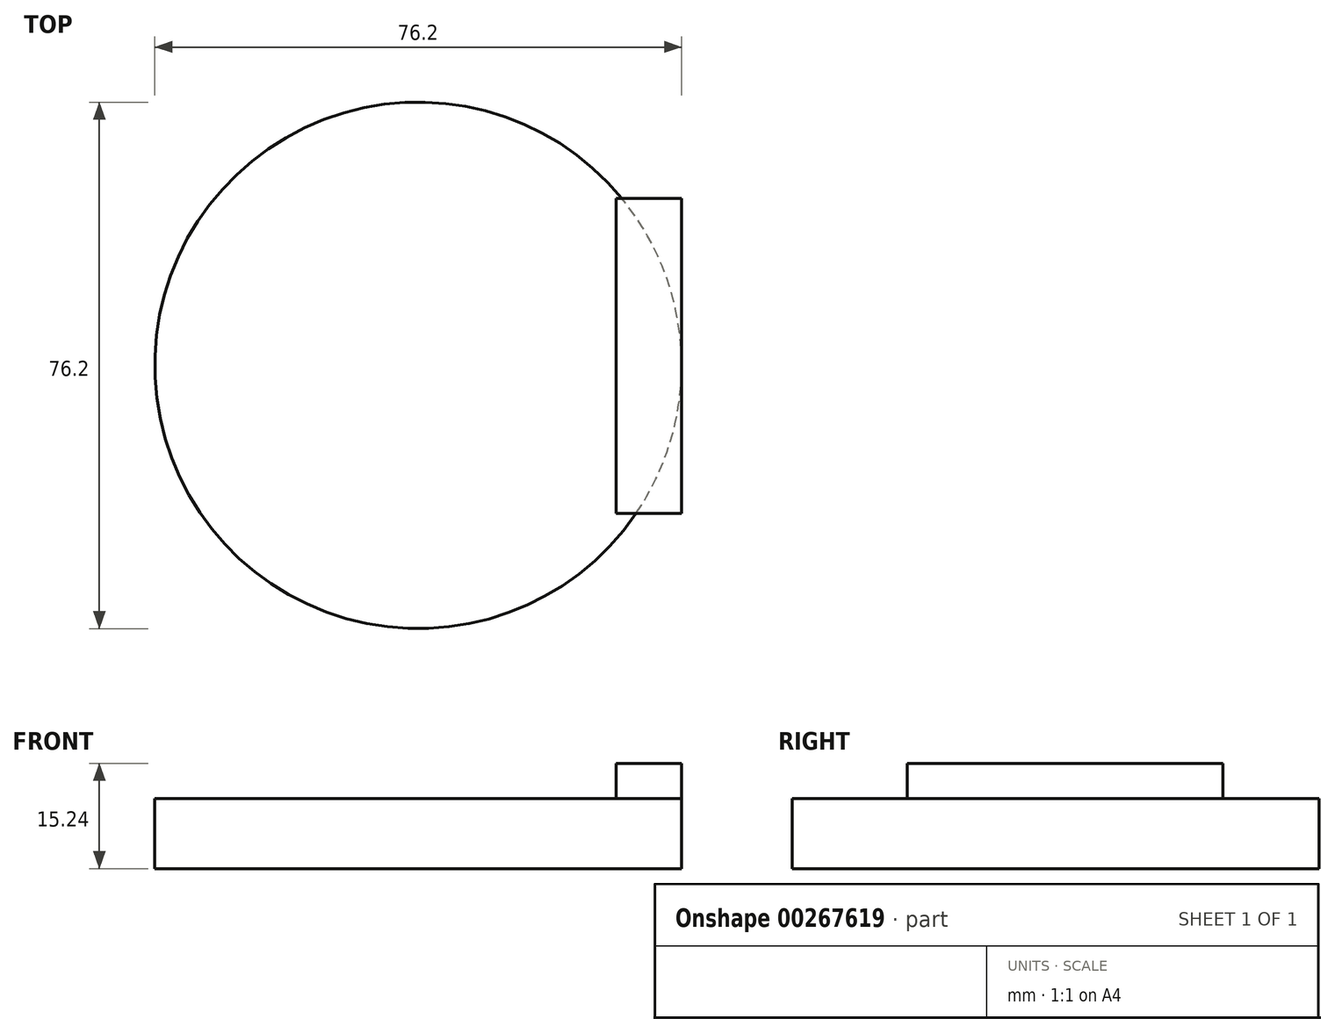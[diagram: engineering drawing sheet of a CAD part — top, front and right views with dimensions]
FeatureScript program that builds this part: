
annotation { "Feature Type Name" : "Feature", "Feature Type Description" : "" }
export const myFeature = defineFeature(function(context is Context, id is Id, definition is map)
    precondition{}
    {
        {
            var Q0;
            Q0=qCreatedBy(makeId("Top.planeOp"),FACE);
            var sketch = newSketch(context, id + "F0", { "sketchPlane" : qUnion([Q0])});
            skCircle(sketch, "E0", {"center": v(0, 0) * mm, "radius": 38.1 * mm});
            skSolve(sketch);
        }
        {
            var Q0;
            Q0 = qSketchRegion(id + "F0", true);
            extrude(context, id + "F1", {"entities" : qUnion([Q0]), "depth" : 10.16 * mm});
        }
        {
            var Q0;
            Q0=makeQuery(id+"F1.opExtrude","CAP_FACE",FACE,{"disambiguationData":[OSD([sQuery(id+"F0.wireOp",EDGE,"E0")])],"isStart":false});
            var sketch = newSketch(context, id + "F2", { "sketchPlane" : qUnion([Q0])});
            skLineSegment(sketch, "E1", {"start": v(38.1, 0) * mm, "end": v(38.1, 24.19) * mm});
            skLineSegment(sketch, "E2", {"start": v(38.1, 24.19) * mm, "end": v(38.1, -21.64) * mm});
            skLineSegment(sketch, "E3.bottom", {"start": v(38.1, 24.19) * mm, "end": v(28.6, 24.19) * mm});
            skLineSegment(sketch, "E3.top", {"start": v(38.1, -21.45) * mm, "end": v(28.6, -21.45) * mm});
            skLineSegment(sketch, "E3.left", {"start": v(38.1, 24.19) * mm, "end": v(38.1, -21.45) * mm});
            skLineSegment(sketch, "E3.right", {"start": v(28.6, 24.19) * mm, "end": v(28.6, -21.45) * mm});
            skSolve(sketch);
        }
        {
            var Q0;
            Q0 = qSketchRegion(id + "F2", true);
            extrude(context, id + "F3", {"entities" : qUnion([Q0]), "operationType" : NewBodyOperationType.ADD, "depth" : 5.08 * mm});
        }
    });
